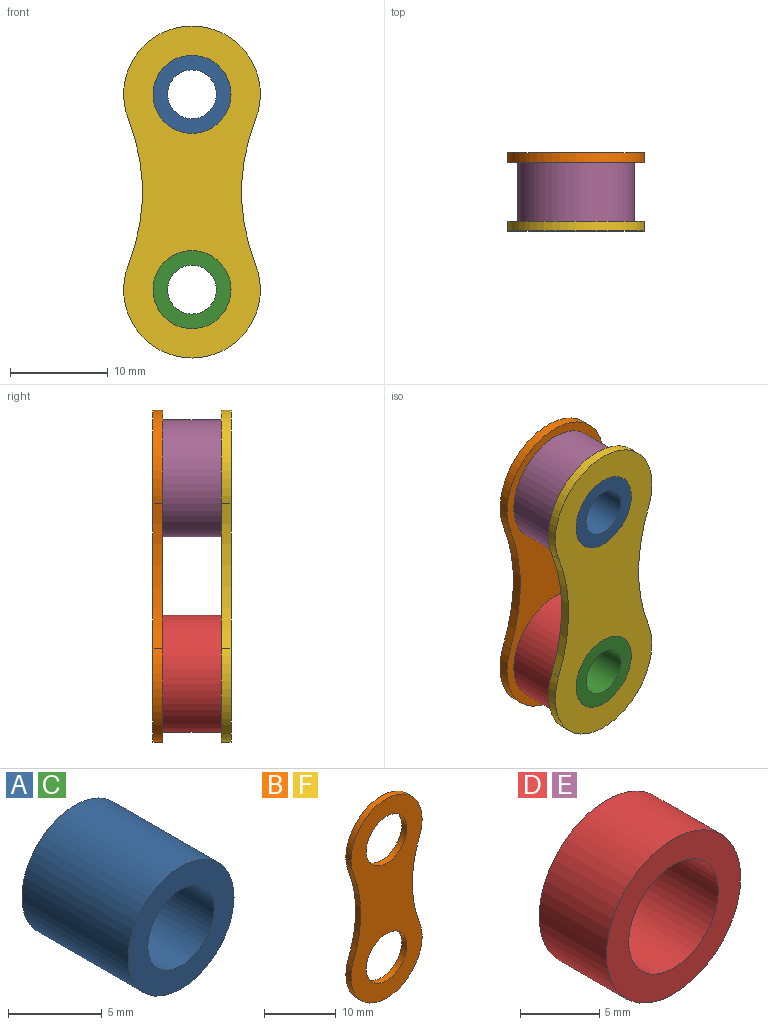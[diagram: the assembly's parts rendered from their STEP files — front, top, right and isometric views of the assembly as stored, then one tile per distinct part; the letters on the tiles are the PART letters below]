
ASSEMBLY  parts=6 mates=6
PART A: 4 faces, bbox 8x8x8 mm
  f0: cylinder r=2.5mm len=8mm, axis (0,1,0), area 125.7mm2, adj f2,f3
  f1: cylinder r=4mm len=8mm, axis (0,1,0), area 201.1mm2, adj f2,f3
  f2: plane 8x8mm, normal (0,-1,0), area 30.6mm2, adj f0,f1
  f3: plane 8x8mm, normal (0,1,0), area 30.6mm2, adj f0,f1
PART B: 8 faces, bbox 14x1x34 mm
  f0: cylinder r=20mm len=14.82mm, axis (0,1,0), area 15.2mm2, adj f1,f5,f6,f7
  f1: cylinder r=7mm len=14mm, axis (0,1,0), area 27.3mm2, adj f0,f2,f6,f7
  f2: cylinder r=20mm len=14.82mm, axis (0,1,0), area 15.2mm2, adj f1,f5,f6,f7
  f3: cylinder r=4mm len=8mm, axis (0,1,0), area 25.1mm2, adj f6,f7
  f4: cylinder r=4mm len=8mm, axis (0,1,0), area 25.1mm2, adj f6,f7
  f5: cylinder r=7mm len=14mm, axis (0,1,0), area 27.3mm2, adj f0,f2,f6,f7
  f6: plane 34x14mm, normal (0,-1,0), area 288.7mm2, adj f0,f1,f2,f3,f4,f5
  f7: plane 34x14mm, normal (0,1,0), area 288.7mm2, adj f0,f1,f2,f3,f4,f5
PART C: same geometry as A
PART D: 4 faces, bbox 12x6x12 mm
  f0: cylinder r=4mm len=8mm, axis (0,1,0), area 150.8mm2, adj f2,f3
  f1: cylinder r=6mm len=12mm, axis (0,1,0), area 226.2mm2, adj f2,f3
  f2: plane 12x12mm, normal (0,-1,0), area 62.8mm2, adj f0,f1
  f3: plane 12x12mm, normal (0,1,0), area 62.8mm2, adj f0,f1
PART E: same geometry as D
PART F: same geometry as B
PLACE A rot(axis=(0,1,0),0deg) t=(93.19,23.96,18.53)mm
PLACE B t=(50.99,23.96,-15.28)mm
PLACE C rot(axis=(0,1,0),0deg) t=(93.19,23.96,-1.47)mm
PLACE D t=(33.84,22.96,-26.49)mm
PLACE E rot(axis=(0,1,0),153.7deg) t=(-46.82,22.96,74.59)mm
PLACE F t=(50.99,16.96,-15.28)mm
MATE fastened C.f0 <-> D.f0  axis (0,1,0) through (2.97,19.96,23.46)mm
MATE fastened A.f0 <-> F.f3  axis (0,1,0) through (2.97,15.96,43.46)mm
MATE fastened C.f0 <-> F.f1  axis (0,-1,0) through (2.97,15.96,23.46)mm
MATE revolute E.f0 <-> B.f3  axis (0,1,0) through (2.97,22.96,43.46)mm
MATE fastened A.f0 <-> B.f3  axis (0,1,0) through (2.97,23.96,43.46)mm
MATE fastened C.f0 <-> B.f1  axis (0,1,0) through (2.97,23.96,23.46)mm
